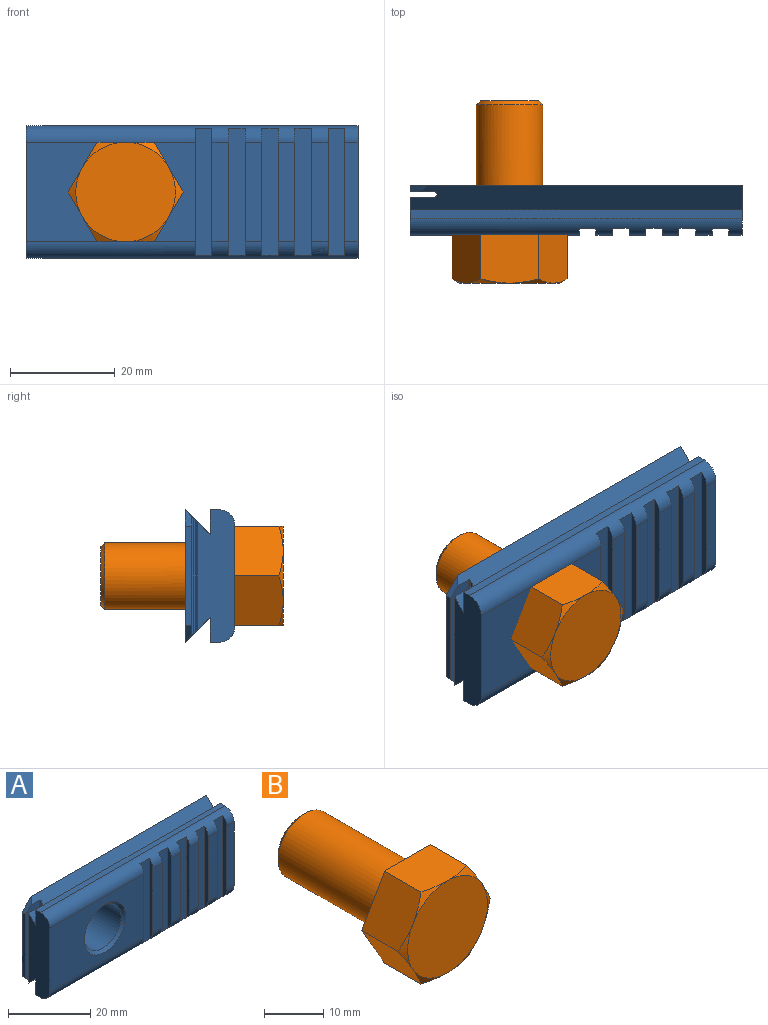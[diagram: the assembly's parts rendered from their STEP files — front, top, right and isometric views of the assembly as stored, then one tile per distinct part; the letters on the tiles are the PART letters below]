
ASSEMBLY  parts=2 mates=1
PART A: 42 faces, bbox 63.5x9.5x25.4 mm
  f0: plane 32.39x19.05mm, normal (0,-1,0), area 456.6mm2, adj f3,f18,f31,f32,f34
  f1: plane 24.13x1.27mm, normal (-1,0,0), area 28.7mm2, adj f2,f4,f31,f32
  f2: plane 24.13x3.18mm, normal (0,-1,0), area 76.6mm2, adj f1,f3,f31,f32
  f3: plane 24.13x1.27mm, normal (1,0,0), area 28.7mm2, adj f0,f2,f31,f32
  f4: plane 19.05x3.18mm, normal (0,-1,0), area 60.5mm2, adj f1,f7,f31,f32
  f5: plane 24.13x1.27mm, normal (-1,0,0), area 28.7mm2, adj f6,f8,f31,f32
  f6: plane 24.13x3.18mm, normal (0,-1,0), area 76.6mm2, adj f5,f7,f31,f32
  f7: plane 24.13x1.27mm, normal (1,0,0), area 28.7mm2, adj f4,f6,f31,f32
  f8: plane 19.05x3.18mm, normal (0,-1,0), area 60.5mm2, adj f5,f11,f31,f32
  f9: plane 24.13x1.27mm, normal (-1,0,0), area 28.7mm2, adj f10,f12,f31,f32
  f10: plane 24.13x3.18mm, normal (0,-1,0), area 76.6mm2, adj f9,f11,f31,f32
  f11: plane 24.13x1.27mm, normal (1,0,0), area 28.7mm2, adj f8,f10,f31,f32
  f12: plane 19.05x3.18mm, normal (0,-1,0), area 60.5mm2, adj f9,f15,f31,f32
  f13: plane 24.13x1.27mm, normal (-1,0,0), area 28.7mm2, adj f14,f16,f31,f32
  f14: plane 24.13x3.18mm, normal (0,-1,0), area 76.6mm2, adj f13,f15,f31,f32
  f15: plane 24.13x1.27mm, normal (1,0,0), area 28.7mm2, adj f12,f14,f31,f32
  f16: plane 19.05x3.18mm, normal (0,-1,0), area 60.5mm2, adj f13,f31,f32,f41
  f17: plane 25.4x9.53mm, normal (1,0,0), area 214.9mm2, adj f26,f27,f28,f29,f31,f32,f35,f36
  f18: plane 25.4x7.24mm, normal (-1,0,0), area 162.1mm2, adj f0,f19,f26,f27,f31,f32,f35,f36
  f19: plane 20.83x4.76mm, normal (0,1,0), area 99.2mm2, adj f18,f22,f36,f38
  f20: plane 22.23x0.38mm, normal (-1,0,0), area 8.3mm2, adj f22,f23,f36,f38
  f21: plane 22.86x4.76mm, normal (0,-1,0), area 105.2mm2, adj f23,f24,f25,f33,f36,f38
  f22: cylinder r=0.32mm len=21.46mm, axis (0,0,1), area 10.5mm2, adj f19,f20,f36,f38
  f23: cylinder r=0.32mm len=22.86mm, axis (0,0,-1), area 11.3mm2, adj f20,f21,f36,f38
  f24: plane 3.18x3.18mm, normal (-0.71,0,-0.71), area 4.6mm2, adj f21,f25,f29,f36
  f25: plane 19.05x1.27mm, normal (-1,0,0), area 24.2mm2, adj f21,f24,f29,f33
  f26: plane 63.5x1.59mm, normal (0,0,-1), area 100.8mm2, adj f17,f18,f31,f35
  f27: plane 63.5x1.59mm, normal (0,0,1), area 100.8mm2, adj f17,f18,f32,f37
  f28: plane 19.05x2.54mm, normal (0,-1,0), area 48.4mm2, adj f17,f31,f32,f39
  f29: plane 63.5x25.4mm, normal (0,1,0), area 1476.1mm2, adj f17,f24,f25,f30,f33,f36,f38
  f30: cylinder r=6.35mm len=12.7mm, axis (0,-1,0), area 348.4mm2, adj f29,f34
  f31: cylinder r=3.17mm len=63.5mm, axis (-1,0,0), area 270mm2, adj f0,f1,f2,f3,f4,f5,f6,f7
  f32: cylinder r=3.17mm len=63.5mm, axis (1,0,0), area 270mm2, adj f0,f1,f2,f3,f4,f5,f6,f7
  f33: plane 3.18x3.18mm, normal (-0.71,0,0.71), area 4.6mm2, adj f21,f25,f29,f38
  f34: cone r=6.35mm half-angle=45deg, axis (0,-1,0), area 47.6mm2, adj f0,f30
  f35: plane 63.5x4.76mm, normal (0,1,0), area 302.4mm2, adj f17,f18,f26,f36
  f36: plane 63.5x4.76mm, normal (0,-0.71,-0.71), area 415.9mm2, adj f17,f18,f19,f20,f21,f22,f23,f24
  f37: plane 63.5x4.76mm, normal (0,1,0), area 302.4mm2, adj f17,f18,f27,f38
  f38: plane 63.5x4.76mm, normal (0,-0.71,0.71), area 415.9mm2, adj f17,f18,f19,f20,f21,f22,f23,f29
  f39: plane 24.13x1.27mm, normal (-1,0,0), area 28.7mm2, adj f28,f31,f32,f40
  f40: plane 24.13x3.18mm, normal (0,-1,0), area 76.6mm2, adj f31,f32,f39,f41
  f41: plane 24.13x1.27mm, normal (1,0,0), area 28.7mm2, adj f16,f31,f32,f40
PART B: 18 faces, bbox 22x34.9x22 mm
  f0: plane 9.53x9.53mm, normal (-0.87,0,-0.5), area 101.6mm2, adj f1,f5,f6,f11,f15
  f1: plane 11.01x9.53mm, normal (0,0,-1), area 101.6mm2, adj f0,f2,f6,f14,f15
  f2: plane 9.53x9.53mm, normal (0.87,0,-0.5), area 101.6mm2, adj f1,f3,f6,f13,f14
  f3: plane 9.53x9.53mm, normal (0.87,0,0.5), area 101.6mm2, adj f2,f4,f6,f12,f13
  f4: plane 11.01x9.53mm, normal (0,0,1), area 101.6mm2, adj f3,f5,f6,f10,f12
  f5: plane 9.53x9.53mm, normal (-0.87,0,0.5), area 101.6mm2, adj f0,f4,f6,f10,f11
  f6: plane 22x19.05mm, normal (0,1,0), area 166.5mm2, adj f0,f1,f2,f3,f4,f5,f17
  f7: cylinder r=6.35mm len=24.13mm, axis (0,-1,0), area 962.7mm2, adj f9,f17
  f8: plane 11.18x11.18mm, normal (0,1,0), area 98.1mm2, adj f9
  f9: cone r=5.59mm half-angle=45deg, axis (0,-1,0), area 40.4mm2, adj f7,f8
  f10: cone r=9.53mm half-angle=60deg, axis (0,1,0), area 5.6mm2, adj f4,f5,f16
  f11: cone r=9.53mm half-angle=60deg, axis (0,1,0), area 5.6mm2, adj f0,f5,f16
  f12: cone r=9.53mm half-angle=60deg, axis (0,1,0), area 5.6mm2, adj f3,f4,f16
  f13: cone r=9.53mm half-angle=60deg, axis (0,1,0), area 5.6mm2, adj f2,f3,f16
  f14: cone r=9.53mm half-angle=60deg, axis (0,1,0), area 5.6mm2, adj f1,f2,f16
  f15: cone r=9.53mm half-angle=60deg, axis (0,1,0), area 5.6mm2, adj f0,f1,f16
  f16: plane 19.05x19.05mm, normal (0,-1,0), area 285mm2, adj f10,f11,f12,f13,f14,f15
  f17: torus R=6.86mm, axis (0,-1,0), area 32.8mm2, adj f6,f7
PLACE A at identity fixed
PLACE B t=(-12.7,-9.24,0)mm
MATE fastened B.f7 <-> A.f30  axis (0,-1,0) through (-12.7,-8.73,0)mm
